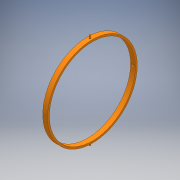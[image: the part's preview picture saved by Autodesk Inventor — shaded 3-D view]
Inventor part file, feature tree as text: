
AUTODESK INVENTOR PART (.ipt)
format: ipt  version: 2018 (Build 220112000, 112)  size: 161,280 bytes
history: native  units: mm
features: extrude x6, sketch x6, plane x4, other x1, mirror x1, projected_geometry x1
ambient origin geometry x8: Origin, YZ Plane, XZ Plane, XY Plane, X Axis, Y Axis, Z Axis, Center Point
bodies: Solid1 (feature_tree)
feature tree (19):
  extrude  "Extrusion1"  Depth=188.0mm
  plane  "Work Plane1"
  extrude  "Extrusion2"  Depth=10.0mm
  plane  "Work Plane2"
  extrude  "Extrusion3"  Depth=230.0mm TaperAngle=0.0deg
  plane  "Work Plane3"
  extrude  "Extrusion4"  Depth=5.0mm TaperAngle=0.0deg
  other  "Work Axis1"
  plane  "Work Plane4"
  extrude  "Extrusion5"  Depth=6.0mm
  mirror  "Mirror1"
  extrude  "Extrusion6"  Depth=3.0mm
  sketch  "Sketch1"  dims[d0=180.0mm d1=188.0mm]
  sketch  "Sketch2"  dims[d2=10.0mm d3=0.0mm d4=6.0mm]
  projected_geometry  "Projected Loop1"
  sketch  "Sketch3"  dims[d5=3.0mm d6=230.0mm d7=0.0mm]
  sketch  "Sketch4"  dims[d8=6.0mm d9=5.0mm d10=0.0mm]
  sketch  "Sketch5"  dims[d11=-4.0mm d12=6.0mm]
  sketch  "Sketch6"  dims[d13=5.0mm d14=0.0mm d15=3.0mm d16=12.0mm d17=0.0mm d18=8.0mm d19=0.0mm]
